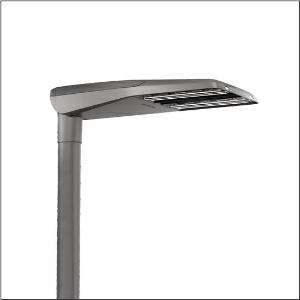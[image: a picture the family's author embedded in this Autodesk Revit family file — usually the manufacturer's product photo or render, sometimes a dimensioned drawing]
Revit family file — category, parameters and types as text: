
# Revit family: streetlight_sl_11_iq_midi___st1_0ab_5xc3n51f08me_d360
name_source: partatom
category: Lighting Fixtures
units: mm (PartAtom-declared; Revit-internal decimal feet)

## family parameters
Cut with Voids When Loaded = No
Host = Face
Light Source = No
Part Type = Normal
Room Calculation Point = No
Round Connector Dimension = Use Diameter
Shared = No

## types (1)
- --- (1 x LED, 15260 lm, 124.7 W, 3000K)
    Apparent Load = 125 VA
    CIE Flux Codes = 29 63 95 100 100
    Color Rendering = 70
    Color Temperature = 3000K
    Default Elevation = 1800 mm
    Description = Streetlight SL 11 iQ midi, mast luminaire, primary light control with 3 zone facetted reflector, of plastic, silver coated, highly specular, primary optical cover: cover, of PMMA, transparent, light distribution: ST1.0aB, light emission: direct distribution, primary light characteristic: asymmetric, installation type: post-top, side-entry, LED, High Power LED, rated luminous flux: 15.260lm, luminous efficacy: 122lm/W, light colour: 730, colour temperature: 3000K, control: optimised constant luminous flux control (CLO 2.0), Street-Remote, Desk-Remote (wireless, voltage-free reading and setting of iQ features in the workshop via application-optimized NFC function/RFID function), Light-Fading, Smart-Wire, Night-Set, Lumen-Switch, Temp-Guard, Auto-Match, with cable H07RN-F 5x 1.5mm², mains connection: 230..240V, AC, 50/60Hz, connection cable pre-assembled, cable length: 12,5m, start of lifetime: 125W, end of service life: 132W, reduction: 57W, luminaire housing, of diecast aluminium, powder-coated, Siteco® metallic grey (DB 702S), please order mast flange separately, inclination adjustable without tools: 0°, 5°, 10°, 15° (post-top) | 0°, -5°, -10°, -15° (side-entry), sealing non-destructively replaceable, multi-level sealing system, length: 780mm, width: 376mm, height: 118mm, mast flange for spigot size: 42mm (side-entry): 5XC10008XM4, 60/48mm (side-entry/post-top): 5XC10108XM2, 76/60mm (side-entry/post-top): 5XC10108XM1, equipment: Power, protection rating (complete): IP66, insulation class (complete): insulation class II (safety insulation), certification: CE, ENEC, VDE, impact resistance: IK09, permissible operating ambient temperature for outdoor applications: -25..+50°C, standard-compliant lighting for roads and squares, Environmental Product Declaration (EPD) tested and certified by an independent institute, packaging unit: 1 piece

Light Distribution: ST1.0aB
    Height = 118 mm
    Lamp = 1 x LED
    Lamp Light Flux = 15260 lm
    Lamp Power = 124.7 W
    Lamp count = 1
    Length = 780 mm
    Luminous efficacy = 122 lm/W
    Manufacturer = Siteco
    ModVariant = No
    Model = 5XC3N51F08ME
    Number of Poles = 1
    OnlyDefault = Yes
    Power Factor = 1
    Product Name = Streetlight SL 11 iQ midi | ST1.0aB
    Product group = mast luminaire | pylon top
    ProductGroupID = 6100
    Protection Class = Protection class II
    Protection Degree = IP 66
    RLX_Detail_Level = 1
    RLX_Emergency_Light_Flux = 0 lm
    RLX_Emergency_Type = 0
    RLX_Emergency_Type_DB = No
    RlxData = <blob elided: 70173 chars, md5=7cd7aaee>
    Socket = socket
    Standby Power = 0 W
    System Light Flux = 15260 lm
    System Power = 125 W
    Type Comments = factory setting: luminous flux: 100 % | dim-lin: 254 | 557 mA
    Type Image = l_1005960.jpg
    URL = http://relux.com
    VarID = @adj_038823
    Voltage = 0 V
    Weight = 0.00 kg
    Width = 376 mm

## geometry (parser evidence)
native form markers: Blend x4, Sweep x9
no freeform markers — native parametric forms only
